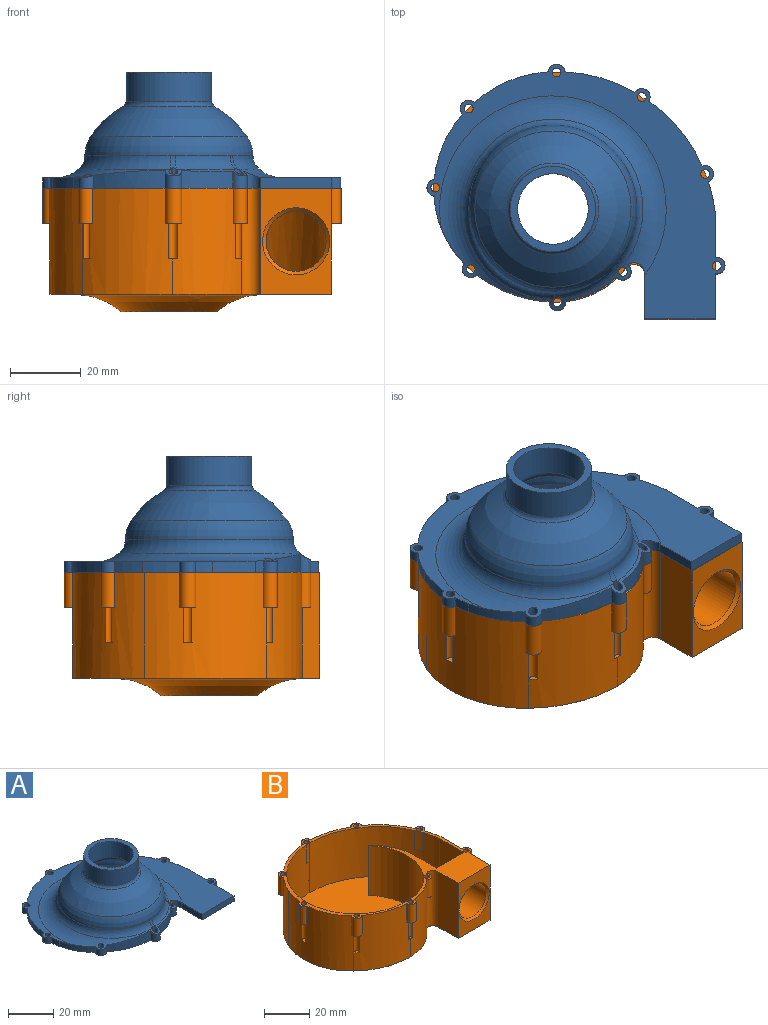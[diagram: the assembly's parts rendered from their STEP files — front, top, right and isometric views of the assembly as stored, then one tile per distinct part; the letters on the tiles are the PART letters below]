
ASSEMBLY  parts=2 mates=1
PART A: 57 faces, bbox 91.2x84.9x33 mm
  f0: cylinder r=35.31mm len=7.96mm, axis (0,0,-1), area 28.7mm2, adj f2,f8,f24,f55
  f1: cylinder r=37mm len=3.39mm, axis (0,0,-1), area 10.4mm2, adj f3,f10,f24,f52
  f2: plane 84.43x72.1mm, normal (0,0,1), area 1372.6mm2, adj f0,f3,f4,f5,f6,f7,f8,f9
  f3: torus R=32.11mm, axis (0,0,1), area 955.5mm2, adj f1,f2,f4,f10,f11,f12,f13,f14
  f4: torus R=32.11mm, axis (0,0,1), area 0.1mm2, adj f2,f3,f15
  f5: cylinder r=45.31mm len=19.86mm, axis (0,0,-1), area 62.6mm2, adj f2,f6,f23,f24
  f6: cylinder r=2.34mm len=4.68mm, axis (0,0,-1), area 21mm2, adj f2,f5,f7,f24
  f7: cylinder r=35.31mm len=20.98mm, axis (0,0,-1), area 69.3mm2, adj f2,f6,f8,f24
  f8: cylinder r=2.34mm len=3.92mm, axis (0,0,-1), area 21.4mm2, adj f0,f2,f7,f24
  f9: cylinder r=2.34mm len=4.35mm, axis (0,0,-1), area 16.8mm2, adj f2,f24,f53,f56
  f10: cylinder r=2.34mm len=4.2mm, axis (0,0,-1), area 27.3mm2, adj f1,f3,f11,f24
  f11: cylinder r=37mm len=20.39mm, axis (0,0,-1), area 97.6mm2, adj f3,f10,f12,f24
  f12: cylinder r=2.34mm len=5.1mm, axis (0,0,-1), area 41.9mm2, adj f3,f11,f13,f24
  f13: cylinder r=25mm len=14.5mm, axis (0,0,-1), area 79.3mm2, adj f3,f12,f14,f24
  f14: cylinder r=2.34mm len=4.8mm, axis (0,0,-1), area 38.4mm2, adj f3,f13,f24,f34
  f15: plane 12.85x3.01mm, normal (-1,0,0), area 38.5mm2, adj f2,f4,f16,f24,f34
  f16: plane 20x3mm, normal (0,-1,0), area 60mm2, adj f2,f15,f17,f24
  f17: plane 12.69x3mm, normal (1,0,0), area 38.1mm2, adj f2,f16,f18,f24
  f18: cylinder r=2.34mm len=4.69mm, axis (0,0,-1), area 24.8mm2, adj f2,f17,f19,f24
  f19: plane 12.7x3mm, normal (1,0,0), area 38.1mm2, adj f2,f18,f20,f24
  f20: cylinder r=45.31mm len=8.83mm, axis (0,0,-1), area 27.2mm2, adj f2,f19,f21,f24
  f21: cylinder r=2.34mm len=4.52mm, axis (0,0,-1), area 21.8mm2, adj f2,f20,f22,f24
  f22: cylinder r=45.31mm len=18.43mm, axis (0,0,-1), area 72.4mm2, adj f2,f21,f23,f24
  f23: cylinder r=2.34mm len=4.28mm, axis (0,0,-1), area 21.6mm2, adj f2,f5,f22,f24
  f24: plane 84.43x72.1mm, normal (0,0,-1), area 2326.2mm2, adj f0,f1,f5,f6,f7,f8,f9,f10
  f25: cylinder r=1.25mm len=5.48mm, axis (0,0,1), area 38.5mm2, adj f3,f24,f48
  f26: cylinder r=1.25mm len=5.8mm, axis (0,0,1), area 38mm2, adj f3,f24,f39,f51
  f27: cylinder r=1.25mm len=3.95mm, axis (0,0,1), area 28.3mm2, adj f3,f24
  f28: cylinder r=1.25mm len=3mm, axis (0,0,1), area 23.6mm2, adj f2,f24
  f29: cylinder r=1.25mm len=3mm, axis (0,0,1), area 23.6mm2, adj f2,f24
  f30: cylinder r=1.25mm len=3mm, axis (0,0,1), area 23.6mm2, adj f2,f24
  f31: cylinder r=1.25mm len=3mm, axis (0,0,1), area 23.6mm2, adj f2,f24
  f32: cylinder r=1.25mm len=3mm, axis (0,0,1), area 23.6mm2, adj f2,f24
  f33: cylinder r=1.25mm len=3mm, axis (0,0,1), area 23.6mm2, adj f2,f24
  f34: cylinder r=3mm len=4.85mm, axis (0,0,1), area 26.1mm2, adj f3,f14,f15,f24
  f35: cylinder r=25mm len=50mm, axis (0,0,1), area 450.7mm2, adj f24,f38
  f36: cylinder r=21.75mm len=43.5mm, axis (0,0,-1), area 865.3mm2, adj f37,f40
  f37: torus R=6.5mm, axis (0,0,-1), area 398.5mm2, adj f36,f38
  f38: cone r=20.22mm half-angle=89.2deg, axis (0,0,-1), area 678.8mm2, adj f35,f37
  f39: cone r=23.81mm half-angle=16.7deg, axis (0,0,-1), area 0mm2, adj f26
  f40: torus R=0.55mm, axis (0,0,-1), area 1598.6mm2, adj f36,f41
  f41: torus R=13.04mm, axis (0,0,-1), area 169mm2, adj f40,f42
  f42: cylinder r=10mm len=20mm, axis (0,0,-1), area 543mm2, adj f41,f43
  f43: plane 24.18x24.18mm, normal (0,0,1), area 145.1mm2, adj f42,f44
  f44: cylinder r=12.09mm len=24.18mm, axis (0,0,-1), area 637.6mm2, adj f43,f45
  f45: torus R=13.98mm, axis (0,0,-1), area 134mm2, adj f44,f46
  f46: revolved ~44.28x44.28mm, area 1410.8mm2, adj f45,f47
  f47: torus R=13.81mm, axis (0,0,1), area 856mm2, adj f46,f48,f49,f50,f51
  f48: bspline ~3.9x2.52mm, area 4.7mm2, adj f25,f47,f49,f50
  f49: torus R=28.81mm, axis (0,0,-1), area 76.3mm2, adj f3,f47,f48,f51
  f50: torus R=28.81mm, axis (0,0,-1), area 563.4mm2, adj f3,f47,f48,f51
  f51: bspline ~3.88x2.07mm, area 6.4mm2, adj f26,f47,f49,f50
  f52: cylinder r=29.08mm len=12.09mm, axis (0,0,-1), area 41.6mm2, adj f1,f2,f3,f24,f54
  f53: cylinder r=1.77mm len=3mm, axis (0,0,-1), area 2.1mm2, adj f2,f9,f24,f54
  f54: cylinder r=32.39mm len=4.77mm, axis (0,0,-1), area 14.5mm2, adj f2,f24,f52,f53
  f55: cylinder r=36.16mm len=10.54mm, axis (0,0,-1), area 32.8mm2, adj f0,f2,f24,f56
  f56: cylinder r=2.09mm len=3mm, axis (0,0,-1), area 1.2mm2, adj f2,f9,f24,f55
PART B: 81 faces, bbox 95.6x91x42 mm
  f0: plane 22.33x22.33mm, normal (0,0,-1), area 11.5mm2, adj f76,f78
  f1: plane 84.43x72.39mm, normal (0,0,1), area 743.6mm2, adj f2,f3,f4,f5,f6,f7,f8,f9
  f2: cylinder r=27.26mm len=27mm, axis (0,0,1), area 576.2mm2, adj f1,f17,f18,f23,f75
  f3: cylinder r=31.5mm len=27mm, axis (0,0,1), area 735.8mm2, adj f1,f5,f18,f74
  f4: cylinder r=23.3mm len=27mm, axis (0,0,1), area 748.9mm2, adj f1,f18,f73,f74
  f5: cylinder r=30mm len=39.85mm, axis (0,0,-1), area 1164.4mm2, adj f1,f3,f6,f18,f35
  f6: cylinder r=33.82mm len=27mm, axis (0,0,1), area 740.3mm2, adj f1,f5,f18,f19,f32
  f7: plane 17x4.51mm, normal (0,1,0), area 41.7mm2, adj f1,f16,f17,f27
  f8: plane 30x20mm, normal (0,-1,0), area 316.5mm2, adj f1,f11,f12,f15,f77
  f9: cylinder r=37mm len=30mm, axis (0,0,-1), area 748.6mm2, adj f1,f10,f15,f20,f40,f41,f42,f43
  f10: cylinder r=25mm len=30mm, axis (0,0,-1), area 576.2mm2, adj f1,f9,f15,f21,f42,f43,f44,f45
  f11: plane 30x12.68mm, normal (-1,0,0), area 380.4mm2, adj f1,f8,f15,f21
  f12: plane 30x30mm, normal (1,0,0), area 829.9mm2, adj f1,f8,f13,f15,f53,f54,f55,f56
  f13: cylinder r=45.31mm len=45mm, axis (0,0,-1), area 1795.8mm2, adj f1,f12,f14,f15,f33,f34,f46,f47
  f14: cylinder r=35.31mm len=32.03mm, axis (0,0,-1), area 1096.4mm2, adj f1,f13,f15,f20,f33,f34,f38,f39
  f15: plane 79.82x70mm, normal (0,0,-1), area 2038mm2, adj f8,f9,f10,f11,f12,f13,f14,f20
  f16: plane 29.06x17.7mm, normal (-1,0,0), area 320.2mm2, adj f1,f7,f19,f23,f26,f28,f31
  f17: plane 29.06x17.7mm, normal (1,0,0), area 320.2mm2, adj f1,f2,f7,f23,f24,f25,f29
  f18: plane 75.41x62.04mm, normal (0,0,1), area 2829mm2, adj f2,f3,f4,f5,f6,f19,f23,f73
  f19: cylinder r=43.82mm len=43.5mm, axis (0,0,1), area 1676.4mm2, adj f1,f6,f16,f18,f23,f32,f48,f49
  f20: cylinder r=30mm len=34.38mm, axis (0,0,-1), area 1042.2mm2, adj f1,f9,f14,f15,f36,f37,f40,f41
  f21: cylinder r=3mm len=30mm, axis (0,0,-1), area 212.3mm2, adj f1,f10,f11,f15,f44,f45
  f22: cylinder r=8.5mm len=21.24mm, axis (0,-1,0), area 744.7mm2, adj f24,f25,f26,f27,f28,f29,f30,f31
  f23: cylinder r=20mm len=17.8mm, axis (-1,0,0), area 204.9mm2, adj f2,f16,f17,f18,f19,f30
  f24: bspline ~8x6.07mm, area 13.3mm2, adj f17,f22,f25
  f25: bspline ~6.33x5.21mm, area 11.7mm2, adj f17,f22,f24,f27
  f26: bspline ~8.56x6.32mm, area 13.3mm2, adj f16,f22,f28
  f27: torus R=13.5mm, axis (0,-1,0), area 110.4mm2, adj f7,f22,f25,f28
  f28: bspline ~6.33x5.21mm, area 11.7mm2, adj f16,f22,f26,f27
  f29: bspline ~7.85x6.71mm, area 12.8mm2, adj f17,f22,f30
  f30: bspline ~19.77x7.94mm, area 58.5mm2, adj f22,f23,f29,f31
  f31: bspline ~6.79x5.45mm, area 12.8mm2, adj f16,f22,f30
  f32: cylinder r=38.21mm len=10mm, axis (0,0,1), area 17.2mm2, adj f1,f6,f19
  f33: cylinder r=2.34mm len=10mm, axis (0,0,1), area 75.9mm2, adj f1,f13,f14,f34
  f34: plane 4.69x2.46mm, normal (0,0,-1), area 6.4mm2, adj f13,f14,f33,f72
  f35: cylinder r=38.21mm len=10mm, axis (0,0,1), area 12.5mm2, adj f1,f5
  f36: cylinder r=2.34mm len=10mm, axis (0,0,1), area 66.4mm2, adj f1,f20,f37
  f37: plane 4.63x2.02mm, normal (0,0,-1), area 5.3mm2, adj f20,f36,f69
  f38: cylinder r=2.34mm len=10mm, axis (0,0,1), area 76.4mm2, adj f1,f14,f39
  f39: plane 4.1x4.09mm, normal (0,0,-1), area 6.4mm2, adj f14,f38,f68
  f40: plane 4.08x3.86mm, normal (0,0,-1), area 6mm2, adj f9,f20,f41,f66
  f41: cylinder r=2.34mm len=10mm, axis (0,0,1), area 72.9mm2, adj f1,f9,f20,f40
  f42: cylinder r=2.34mm len=10mm, axis (0,0,1), area 77.3mm2, adj f1,f9,f10,f43
  f43: plane 4.69x2.56mm, normal (0,0,-1), area 6.5mm2, adj f9,f10,f42,f64
  f44: plane 4.03x3.95mm, normal (0,0,-1), area 6.2mm2, adj f10,f21,f45,f62
  f45: cylinder r=2.34mm len=10mm, axis (0,0,1), area 73.3mm2, adj f1,f10,f21,f44
  f46: cylinder r=2.34mm len=10mm, axis (0,0,1), area 76.2mm2, adj f1,f13,f47
  f47: plane 4.39x3.7mm, normal (0,0,-1), area 6.4mm2, adj f13,f46,f60
  f48: cylinder r=38.21mm len=10mm, axis (0,0,1), area 34.6mm2, adj f1,f19,f49,f50
  f49: plane 3.4x1.47mm, normal (0,0,-1), area 0.4mm2, adj f19,f48,f50
  f50: cylinder r=2.34mm len=10mm, axis (0,0,1), area 3mm2, adj f1,f19,f48,f49
  f51: cylinder r=2.34mm len=10mm, axis (0,0,1), area 73.6mm2, adj f1,f13,f52
  f52: plane 4.53x3.2mm, normal (0,0,-1), area 6.1mm2, adj f13,f51,f58
  f53: cylinder r=2.34mm len=10mm, axis (0,0,1), area 81.2mm2, adj f1,f12,f54
  f54: plane 4.69x2.72mm, normal (0,0,-1), area 7mm2, adj f12,f53,f55
  f55: cylinder r=1.25mm len=20mm, axis (0,0,1), area 110.2mm2, adj f1,f12,f54,f56
  f56: plane 2.38x0.87mm, normal (0,0,1), area 1.5mm2, adj f12,f55
  f57: plane 2.43x1.75mm, normal (0,0,1), area 2.6mm2, adj f13,f58
  f58: cylinder r=1.25mm len=20mm, axis (0,0,1), area 118.7mm2, adj f1,f13,f52,f57
  f59: plane 2.26x1.85mm, normal (0,0,1), area 2.3mm2, adj f13,f60
  f60: cylinder r=1.25mm len=20mm, axis (0,0,1), area 116.2mm2, adj f1,f13,f47,f59
  f61: plane 2.19x2.07mm, normal (0,0,1), area 2.5mm2, adj f10,f62
  f62: cylinder r=1.25mm len=20mm, axis (0,0,1), area 117.7mm2, adj f1,f10,f44,f61
  f63: plane 2.49x1.17mm, normal (0,0,1), area 2.2mm2, adj f9,f10,f64
  f64: cylinder r=1.25mm len=20mm, axis (0,0,1), area 115.5mm2, adj f1,f9,f10,f43,f63
  f65: plane 2.25x2.14mm, normal (0,0,1), area 2.7mm2, adj f9,f66
  f66: cylinder r=1.25mm len=20mm, axis (0,0,1), area 119.7mm2, adj f1,f9,f40,f65
  f67: plane 2.08x2.07mm, normal (0,0,1), area 2.3mm2, adj f14,f68
  f68: cylinder r=1.25mm len=20mm, axis (0,0,1), area 116.2mm2, adj f1,f14,f39,f67
  f69: cylinder r=1.25mm len=20mm, axis (0,0,1), area 126.5mm2, adj f1,f20,f37,f70
  f70: plane 2.5x1.7mm, normal (0,0,1), area 3.5mm2, adj f20,f69
  f71: plane 2.5x1.21mm, normal (0,0,1), area 2.3mm2, adj f13,f14,f72
  f72: cylinder r=1.25mm len=20mm, axis (0,0,1), area 116.6mm2, adj f1,f13,f14,f34,f71
  f73: cylinder r=25mm len=27.19mm, axis (0,0,-1), area 789.5mm2, adj f1,f4,f18,f75
  f74: cylinder r=25mm len=27mm, axis (0,0,-1), area 57.8mm2, adj f1,f3,f4,f18
  f75: cylinder r=0.05mm len=27mm, axis (0,0,-1), area 4.1mm2, adj f1,f2,f18,f73
  f76: cylinder r=11mm len=22mm, axis (0,0,-1), area 207.3mm2, adj f0,f18
  f77: cone r=8.5mm half-angle=45deg, axis (0,-1,0), area 80mm2, adj f8,f22
  f78: cylinder r=11.16mm len=22.33mm, axis (0,0,1), area 350.8mm2, adj f0,f79
  f79: plane 26.76x26.76mm, normal (0,0,-1), area 170.6mm2, adj f78,f80
  f80: torus R=26.61mm, axis (0,0,1), area 1783.5mm2, adj f9,f10,f15,f79
PLACE A t=(12.27,33.84,29.1)mm
PLACE B t=(-14.04,-1.7,-0.9)mm fixed
MATE slider A.f18 <-> B.f53  axis (0,0,-1) through (31.34,-16.42,29.1)mm
